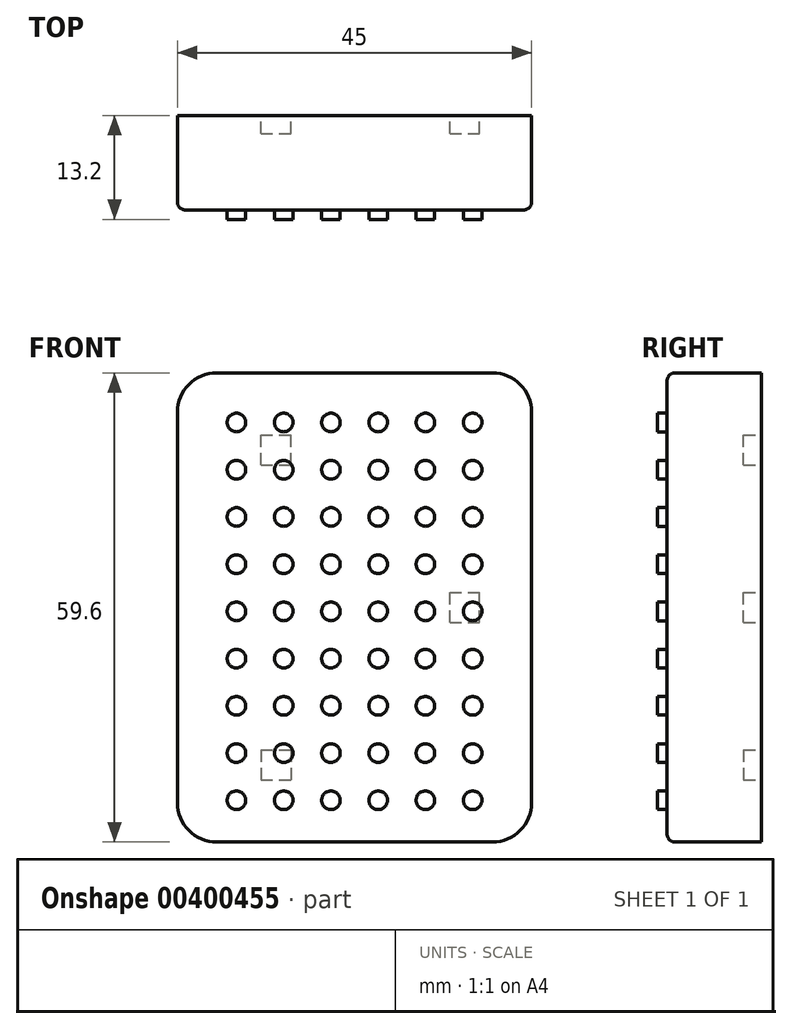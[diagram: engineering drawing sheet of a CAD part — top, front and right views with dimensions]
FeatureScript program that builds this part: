
annotation { "Feature Type Name" : "Feature", "Feature Type Description" : "" }
export const myFeature = defineFeature(function(context is Context, id is Id, definition is map)
    precondition{}
    {
        {
            var Q0;
            Q0=qCreatedBy(makeId("Front.planeOp"),FACE);
            var sketch = newSketch(context, id + "F0", { "sketchPlane" : qUnion([Q0])});
            skLineSegment(sketch, "E0.bottom", {"start": v(-17.5, 29.8) * mm, "end": v(17.5, 29.8) * mm});
            skLineSegment(sketch, "E0.top", {"start": v(-17.5, -29.8) * mm, "end": v(17.5, -29.8) * mm});
            skLineSegment(sketch, "E0.left", {"start": v(-22.5, 24.8) * mm, "end": v(-22.5, -24.8) * mm});
            skLineSegment(sketch, "E0.right", {"start": v(22.5, 24.8) * mm, "end": v(22.5, -24.8) * mm});
            skPoint(sketch, "E0.middle", {"position": v(0, 0) * mm});
            skPoint(sketch, "E1.visualSharp", {"position": v(-22.5, 29.8) * mm});
            skArc(sketch, "E1.filletArc", {"start": v(-17.5, 29.8) * mm, "mid": v(-21.04, 28.34) * mm, "end": v(-22.5, 24.8) * mm});
            skPoint(sketch, "E2.visualSharp", {"position": v(22.5, 29.8) * mm});
            skArc(sketch, "E2.filletArc", {"start": v(22.5, 24.8) * mm, "mid": v(21.04, 28.34) * mm, "end": v(17.5, 29.8) * mm});
            skPoint(sketch, "E3.visualSharp", {"position": v(22.5, -29.8) * mm});
            skArc(sketch, "E3.filletArc", {"start": v(17.5, -29.8) * mm, "mid": v(21.04, -28.34) * mm, "end": v(22.5, -24.8) * mm});
            skPoint(sketch, "E4.visualSharp", {"position": v(-22.5, -29.8) * mm});
            skArc(sketch, "E4.filletArc", {"start": v(-22.5, -24.8) * mm, "mid": v(-21.04, -28.34) * mm, "end": v(-17.5, -29.8) * mm});
            skSolve(sketch);
        }
        {
            var Q0;
            Q0 = qSketchRegion(id + "F0", true);
            extrude(context, id + "F1", {"entities" : qUnion([Q0]), "depth" : 12 * mm});
        }
        {
            var Q0;
            Q0=makeQuery(id+"F1.opExtrude","CAP_FACE",FACE,{"disambiguationData":[OSD([sQuery(id+"F0.wireOp",EDGE,"E0.bottom"),sQuery(id+"F0.wireOp",EDGE,"E0.top"),sQuery(id+"F0.wireOp",EDGE,"E0.left"),sQuery(id+"F0.wireOp",EDGE,"E0.right"),sQuery(id+"F0.wireOp",EDGE,"E1.filletArc"),sQuery(id+"F0.wireOp",EDGE,"E2.filletArc"),sQuery(id+"F0.wireOp",EDGE,"E3.filletArc"),sQuery(id+"F0.wireOp",EDGE,"E4.filletArc")])],"isStart":false});
            fillet(context, id + "F2", {"entities" : qUnion([Q0]), "radius" : 1 * mm, "tangentPropagation" : true, "allowEdgeOverflow" : false});
        }
        {
            var Q0;
            Q0=makeQuery(id+"F1.opExtrude","CAP_FACE",FACE,{"disambiguationData":[OSD([sQuery(id+"F0.wireOp",EDGE,"E0.bottom"),sQuery(id+"F0.wireOp",EDGE,"E0.top"),sQuery(id+"F0.wireOp",EDGE,"E0.left"),sQuery(id+"F0.wireOp",EDGE,"E0.right"),sQuery(id+"F0.wireOp",EDGE,"E1.filletArc"),sQuery(id+"F0.wireOp",EDGE,"E2.filletArc"),sQuery(id+"F0.wireOp",EDGE,"E3.filletArc"),sQuery(id+"F0.wireOp",EDGE,"E4.filletArc")])],"isStart":true});
            var sketch = newSketch(context, id + "F3", { "sketchPlane" : qUnion([Q0])});
            skLineSegment(sketch, "E5.bottom", {"start": v(11.9, 18.1) * mm, "end": v(8.1, 18.1) * mm});
            skLineSegment(sketch, "E5.top", {"start": v(11.9, 21.9) * mm, "end": v(8.1, 21.9) * mm});
            skLineSegment(sketch, "E5.left", {"start": v(11.9, 18.1) * mm, "end": v(11.9, 21.9) * mm});
            skLineSegment(sketch, "E5.right", {"start": v(8.1, 18.1) * mm, "end": v(8.1, 21.9) * mm});
            skPoint(sketch, "E5.middle", {"position": v(10, 20) * mm});
            skLineSegment(sketch, "E6", {"start": v(0, 0) * mm, "end": v(40.58, 0) * mm, "construction": true});
            skPoint(sketch, "E6.endSnap0", {"position": v(22.5, 0) * mm});
            skLineSegment(sketch, "E7", {"start": v(0, 0) * mm, "end": v(0, 50.1) * mm, "construction": true});
            skLineSegment(sketch, "E8.bottom", {"start": v(-12.1, -1.9) * mm, "end": v(-15.9, -1.9) * mm});
            skLineSegment(sketch, "E8.top", {"start": v(-12.1, 1.9) * mm, "end": v(-15.9, 1.9) * mm});
            skLineSegment(sketch, "E8.left", {"start": v(-12.1, -1.9) * mm, "end": v(-12.1, 1.9) * mm});
            skLineSegment(sketch, "E8.right", {"start": v(-15.9, -1.9) * mm, "end": v(-15.9, 1.9) * mm});
            skPoint(sketch, "E8.middle", {"position": v(-14, 0) * mm});
            skLineSegment(sketch, "E9.MirrorCS", {"start": v(11.9, -18.1) * mm, "end": v(8.1, -18.1) * mm});
            skLineSegment(sketch, "E10.MirrorCS", {"start": v(11.9, -21.9) * mm, "end": v(8.1, -21.9) * mm});
            skLineSegment(sketch, "E11.MirrorCS", {"start": v(8.1, -18.1) * mm, "end": v(8.1, -21.9) * mm});
            skLineSegment(sketch, "E12.MirrorCS", {"start": v(11.9, -18.1) * mm, "end": v(11.9, -21.9) * mm});
            skPoint(sketch, "E13.MirrorP", {"position": v(10, -20) * mm});
            skSolve(sketch);
        }
        {
            var Q0;
            Q0 = qSketchRegion(id + "F3", true);
            extrude(context, id + "F4", {"entities" : qUnion([Q0]), "operationType" : NewBodyOperationType.REMOVE, "oppositeDirection" : true, "depth" : 2.3 * mm});
        }
        {
            var Q0;
            Q0=makeQuery(id+"F1.opExtrude","CAP_FACE",FACE,{"disambiguationData":[OSD([sQuery(id+"F0.wireOp",EDGE,"E0.bottom"),sQuery(id+"F0.wireOp",EDGE,"E0.top"),sQuery(id+"F0.wireOp",EDGE,"E0.left"),sQuery(id+"F0.wireOp",EDGE,"E0.right"),sQuery(id+"F0.wireOp",EDGE,"E1.filletArc"),sQuery(id+"F0.wireOp",EDGE,"E2.filletArc"),sQuery(id+"F0.wireOp",EDGE,"E3.filletArc"),sQuery(id+"F0.wireOp",EDGE,"E4.filletArc")])],"isStart":false});
            var sketch = newSketch(context, id + "F5", { "sketchPlane" : qUnion([Q0])});
            skCircle(sketch, "E14", {"center": v(-15, 23.5) * mm, "radius": 1.18 * mm});
            skCircle(sketch, "E15.0.1.0", {"center": v(-15, 17.5) * mm, "radius": 1.18 * mm});
            skCircle(sketch, "E15.0.2.0", {"center": v(-15, 11.5) * mm, "radius": 1.18 * mm});
            skCircle(sketch, "E15.0.3.0", {"center": v(-15, 5.5) * mm, "radius": 1.18 * mm});
            skCircle(sketch, "E15.0.4.0", {"center": v(-15, -0.5) * mm, "radius": 1.18 * mm});
            skCircle(sketch, "E15.1.0.0", {"center": v(-9, 23.5) * mm, "radius": 1.18 * mm});
            skCircle(sketch, "E15.1.1.0", {"center": v(-9, 17.5) * mm, "radius": 1.18 * mm});
            skCircle(sketch, "E15.1.2.0", {"center": v(-9, 11.5) * mm, "radius": 1.18 * mm});
            skCircle(sketch, "E15.1.3.0", {"center": v(-9, 5.5) * mm, "radius": 1.18 * mm});
            skCircle(sketch, "E15.1.4.0", {"center": v(-9, -0.5) * mm, "radius": 1.18 * mm});
            skCircle(sketch, "E15.2.0.0", {"center": v(-3, 23.5) * mm, "radius": 1.18 * mm});
            skCircle(sketch, "E15.2.1.0", {"center": v(-3, 17.5) * mm, "radius": 1.18 * mm});
            skCircle(sketch, "E15.2.2.0", {"center": v(-3, 11.5) * mm, "radius": 1.18 * mm});
            skCircle(sketch, "E15.2.3.0", {"center": v(-3, 5.5) * mm, "radius": 1.18 * mm});
            skCircle(sketch, "E15.2.4.0", {"center": v(-3, -0.5) * mm, "radius": 1.18 * mm});
            skCircle(sketch, "E15.3.0.0", {"center": v(3, 23.5) * mm, "radius": 1.18 * mm});
            skCircle(sketch, "E15.3.1.0", {"center": v(3, 17.5) * mm, "radius": 1.18 * mm});
            skCircle(sketch, "E15.3.2.0", {"center": v(3, 11.5) * mm, "radius": 1.18 * mm});
            skCircle(sketch, "E15.3.3.0", {"center": v(3, 5.5) * mm, "radius": 1.18 * mm});
            skCircle(sketch, "E15.3.4.0", {"center": v(3, -0.5) * mm, "radius": 1.18 * mm});
            skLineSegment(sketch, "E15.direction1", {"start": v(-15, 23.5) * mm, "end": v(-9, 23.5) * mm, "construction": true});
            skLineSegment(sketch, "E15.direction2", {"start": v(-15, 23.5) * mm, "end": v(-15, 17.5) * mm, "construction": true});
            skCircle(sketch, "E16.0.0.5", {"center": v(-15, -6.5) * mm, "radius": 1.18 * mm});
            skCircle(sketch, "E16.0.0.6", {"center": v(-15, -12.5) * mm, "radius": 1.18 * mm});
            skCircle(sketch, "E16.0.0.7", {"center": v(-15, -18.5) * mm, "radius": 1.18 * mm});
            skCircle(sketch, "E16.0.0.8", {"center": v(-15, -24.5) * mm, "radius": 1.18 * mm});
            skCircle(sketch, "E16.0.1.5", {"center": v(-9, -6.5) * mm, "radius": 1.18 * mm});
            skCircle(sketch, "E16.0.1.6", {"center": v(-9, -12.5) * mm, "radius": 1.18 * mm});
            skCircle(sketch, "E16.0.1.7", {"center": v(-9, -18.5) * mm, "radius": 1.18 * mm});
            skCircle(sketch, "E16.0.1.8", {"center": v(-9, -24.5) * mm, "radius": 1.18 * mm});
            skCircle(sketch, "E16.0.2.5", {"center": v(-3, -6.5) * mm, "radius": 1.18 * mm});
            skCircle(sketch, "E16.0.2.6", {"center": v(-3, -12.5) * mm, "radius": 1.18 * mm});
            skCircle(sketch, "E16.0.2.7", {"center": v(-3, -18.5) * mm, "radius": 1.18 * mm});
            skCircle(sketch, "E16.0.2.8", {"center": v(-3, -24.5) * mm, "radius": 1.18 * mm});
            skCircle(sketch, "E16.0.3.5", {"center": v(3, -6.5) * mm, "radius": 1.18 * mm});
            skCircle(sketch, "E16.0.3.6", {"center": v(3, -12.5) * mm, "radius": 1.18 * mm});
            skCircle(sketch, "E16.0.3.7", {"center": v(3, -18.5) * mm, "radius": 1.18 * mm});
            skCircle(sketch, "E16.0.3.8", {"center": v(3, -24.5) * mm, "radius": 1.18 * mm});
            skCircle(sketch, "E17.0.4.0", {"center": v(9, 23.5) * mm, "radius": 1.18 * mm});
            skCircle(sketch, "E17.0.4.1", {"center": v(9, 17.5) * mm, "radius": 1.18 * mm});
            skCircle(sketch, "E17.0.4.2", {"center": v(9, 11.5) * mm, "radius": 1.18 * mm});
            skCircle(sketch, "E17.0.4.3", {"center": v(9, 5.5) * mm, "radius": 1.18 * mm});
            skCircle(sketch, "E17.0.4.4", {"center": v(9, -0.5) * mm, "radius": 1.18 * mm});
            skCircle(sketch, "E17.0.4.5", {"center": v(9, -6.5) * mm, "radius": 1.18 * mm});
            skCircle(sketch, "E17.0.4.6", {"center": v(9, -12.5) * mm, "radius": 1.18 * mm});
            skCircle(sketch, "E17.0.4.7", {"center": v(9, -18.5) * mm, "radius": 1.18 * mm});
            skCircle(sketch, "E17.0.4.8", {"center": v(9, -24.5) * mm, "radius": 1.18 * mm});
            skCircle(sketch, "E17.0.5.0", {"center": v(15, 23.5) * mm, "radius": 1.18 * mm});
            skCircle(sketch, "E17.0.5.1", {"center": v(15, 17.5) * mm, "radius": 1.18 * mm});
            skCircle(sketch, "E17.0.5.2", {"center": v(15, 11.5) * mm, "radius": 1.18 * mm});
            skCircle(sketch, "E17.0.5.3", {"center": v(15, 5.5) * mm, "radius": 1.18 * mm});
            skCircle(sketch, "E17.0.5.4", {"center": v(15, -0.5) * mm, "radius": 1.18 * mm});
            skCircle(sketch, "E17.0.5.5", {"center": v(15, -6.5) * mm, "radius": 1.18 * mm});
            skCircle(sketch, "E17.0.5.6", {"center": v(15, -12.5) * mm, "radius": 1.18 * mm});
            skCircle(sketch, "E17.0.5.7", {"center": v(15, -18.5) * mm, "radius": 1.18 * mm});
            skCircle(sketch, "E17.0.5.8", {"center": v(15, -24.5) * mm, "radius": 1.18 * mm});
            skSolve(sketch);
        }
        {
            var Q0;
            Q0 = qSketchRegion(id + "F5", true);
            extrude(context, id + "F6", {"entities" : qUnion([Q0]), "operationType" : NewBodyOperationType.ADD, "depth" : 1.2 * mm});
        }
    });
